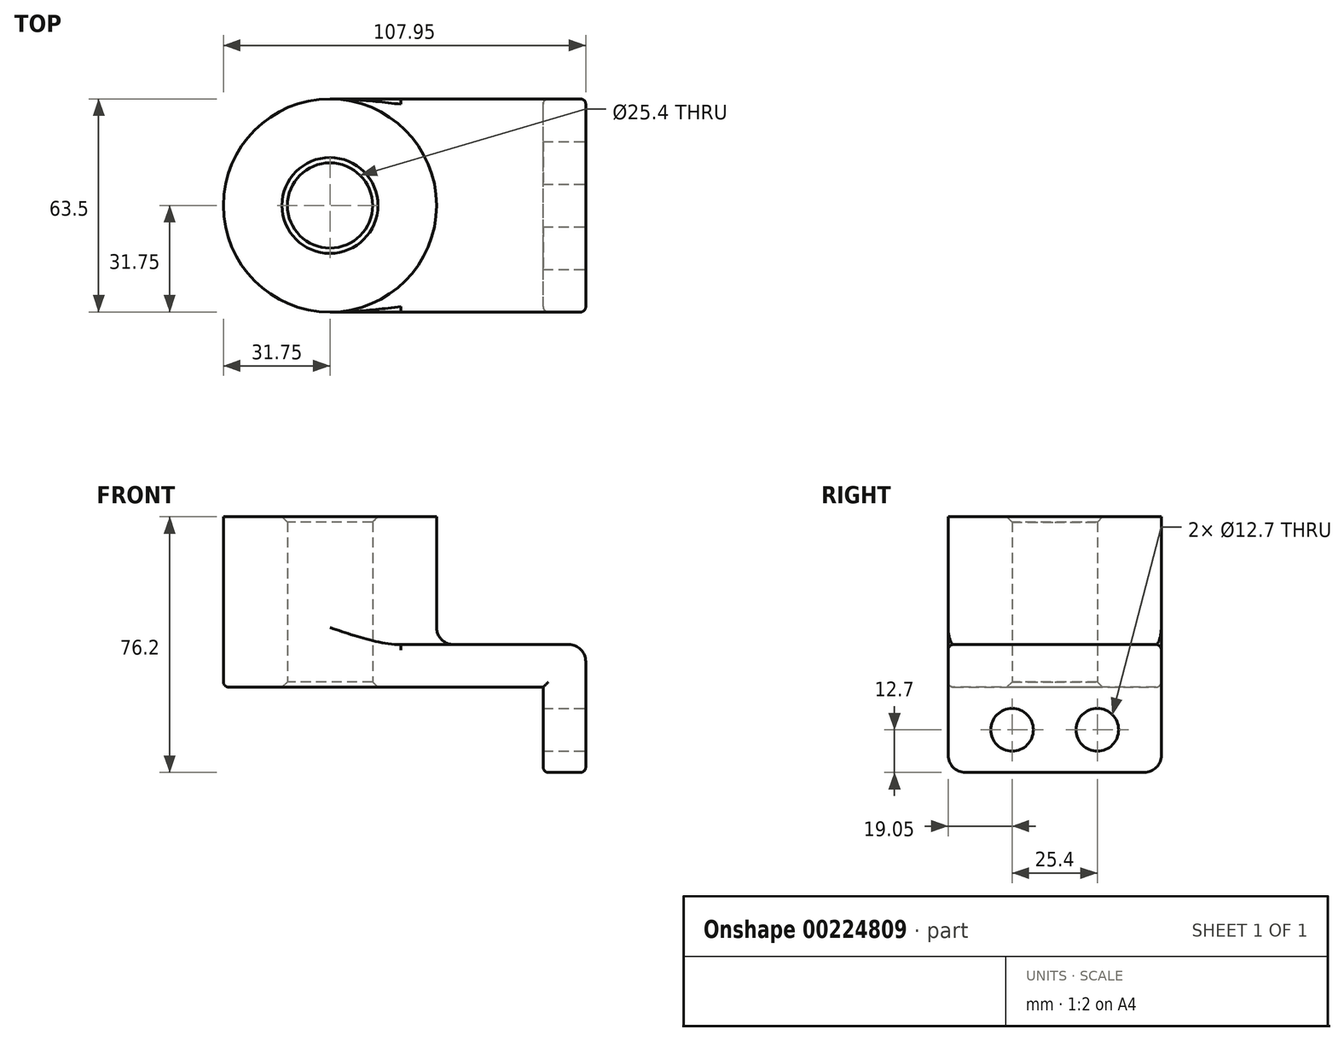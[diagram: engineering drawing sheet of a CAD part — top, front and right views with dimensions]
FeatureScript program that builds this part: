
annotation { "Feature Type Name" : "Feature", "Feature Type Description" : "" }
export const myFeature = defineFeature(function(context is Context, id is Id, definition is map)
    precondition{}
    {
        {
            var Q0;
            Q0=qCreatedBy(makeId("Top.planeOp"),FACE);
            var sketch = newSketch(context, id + "F0", { "sketchPlane" : qUnion([Q0])});
            skLineSegment(sketch, "E0.bottom", {"start": v(38.1, -31.75) * mm, "end": v(-38.1, -31.75) * mm});
            skLineSegment(sketch, "E0.top", {"start": v(38.1, 31.75) * mm, "end": v(-38.1, 31.75) * mm});
            skLineSegment(sketch, "E0.left", {"start": v(38.1, -31.75) * mm, "end": v(38.1, 31.75) * mm});
            skLineSegment(sketch, "E0.right", {"start": v(-38.1, -31.75) * mm, "end": v(-38.1, 31.75) * mm});
            skPoint(sketch, "E0.middle", {"position": v(0, 0) * mm});
            skCircle(sketch, "E1", {"center": v(-38.1, 0) * mm, "radius": 31.75 * mm});
            skCircle(sketch, "E2", {"center": v(-38.1, 0) * mm, "radius": 12.7 * mm});
            skSolve(sketch);
        }
        {
            var Q0;
            Q0 = qSketchRegion(id + "F0", true);
            extrude(context, id + "F1", {"entities" : qUnion([Q0]), "depth" : 12.7 * mm});
        }
        {
            var Q0;
            {var subQ1=sQuery(id+"F0.wireOp",EDGE,"E0.right");var subQ3=sQuery(id+"F0.wireOp",EDGE,"E2");var subQ4=makeQuery(id+"F0.imprint","INTERSECT",VERTEX,{"disambiguationData":[OD(0.0)],"derivedFrom":[subQ1,subQ3]});Q0=makeQuery(id+"F0.imprint","IMPRINT",FACE,{"disambiguationData":[TD([[makeQuery(id+"F0.imprint","IMPRINT",EDGE,{"disambiguationData":[TD([[subQ4,1.0]])],"derivedFrom":subQ3}),-1.0]])]});}
            var Q1;
            {var subQ1=sQuery(id+"F0.wireOp",EDGE,"E0.right");var subQ3=sQuery(id+"F0.wireOp",EDGE,"E2");var subQ4=makeQuery(id+"F0.imprint","INTERSECT",VERTEX,{"disambiguationData":[OD(0.0)],"derivedFrom":[subQ1,subQ3]});Q1=makeQuery(id+"F0.imprint","IMPRINT",FACE,{"disambiguationData":[TD([[makeQuery(id+"F0.imprint","IMPRINT",EDGE,{"disambiguationData":[TD([[subQ4,-1.0]])],"derivedFrom":subQ3}),-1.0]])]});}
            extrude(context, id + "F2", {"entities" : qUnion([Q0, Q1]), "operationType" : NewBodyOperationType.ADD, "depth" : 50.8 * mm});
        }
        {
            var Q0;
            Q0=makeQuery(id+"F1.opExtrude","SWEPT_FACE",FACE,{"disambiguationData":[OSD([sQuery(id+"F0.wireOp",EDGE,"E0.left")])]});
            var sketch = newSketch(context, id + "F3", { "sketchPlane" : qUnion([Q0])});
            skLineSegment(sketch, "E3.bottom", {"start": v(-31.75, 12.7) * mm, "end": v(31.75, 12.7) * mm});
            skLineSegment(sketch, "E3.top", {"start": v(-31.75, -25.4) * mm, "end": v(31.75, -25.4) * mm});
            skLineSegment(sketch, "E3.left", {"start": v(-31.75, 12.7) * mm, "end": v(-31.75, -25.4) * mm});
            skLineSegment(sketch, "E3.right", {"start": v(31.75, 12.7) * mm, "end": v(31.75, -25.4) * mm});
            skCircle(sketch, "E4", {"center": v(-12.7, -12.7) * mm, "radius": 6.35 * mm});
            skLineSegment(sketch, "E5", {"start": v(0, 0) * mm, "end": v(0, -25.4) * mm, "construction": true});
            skCircle(sketch, "E6.MirrorC", {"center": v(12.7, -12.7) * mm, "radius": 6.35 * mm});
            skSolve(sketch);
        }
        {
            var Q0;
            Q0 = qSketchRegion(id + "F3", true);
            extrude(context, id + "F4", {"entities" : qUnion([Q0]), "operationType" : NewBodyOperationType.ADD, "oppositeDirection" : true, "depth" : 12.7 * mm});
        }
        {
            var Q0;
            {var subQ0=sQuery(id+"F0.wireOp",EDGE,"E1");Q0=makeQuery(id+"F2.boolean.opBoolean","INTERSECT",EDGE,{"derivedFrom":[makeQuery(id+"F1.opExtrude","CAP_FACE",FACE,{"disambiguationData":[OSD([sQuery(id+"F0.wireOp",EDGE,"E0.bottom"),sQuery(id+"F0.wireOp",EDGE,"E0.top"),sQuery(id+"F0.wireOp",EDGE,"E0.left"),subQ0,sQuery(id+"F0.wireOp",EDGE,"E2")])],"isStart":false}),makeQuery(id+"F2.opExtrude","SWEPT_FACE",FACE,{"disambiguationData":[OSD([subQ0])]})]});}
            var Q1;
            Q1=makeQuery(id+"F1.opExtrude","CAP_EDGE",EDGE,{"disambiguationData":[OSD([sQuery(id+"F0.wireOp",EDGE,"E0.left")])],"isStart":false});
            var Q2;
            Q2=makeQuery(id+"F4.opExtrude","SWEPT_EDGE",EDGE,{"disambiguationData":[OSD([sQuery(id+"F3.wireOp",EDGE,"E3.top"),sQuery(id+"F3.wireOp",EDGE,"E3.left")])]});
            var Q3;
            Q3=makeQuery(id+"F4.opExtrude","SWEPT_EDGE",EDGE,{"disambiguationData":[OSD([sQuery(id+"F3.wireOp",EDGE,"E3.top"),sQuery(id+"F3.wireOp",EDGE,"E3.right")])]});
            fillet(context, id + "F5", {"entities" : qUnion([Q0, Q1, Q2, Q3]), "radius" : 5.08 * mm, "tangentPropagation" : true, "allowEdgeOverflow" : false});
        }
        {
            var Q0;
            Q0=makeQuery(id+"F1.opExtrude","CAP_EDGE",EDGE,{"disambiguationData":[OSD([sQuery(id+"F0.wireOp",EDGE,"E0.bottom")])],"isStart":false});
            var Q1;
            Q1=makeQuery(id+"F1.opExtrude","CAP_EDGE",EDGE,{"disambiguationData":[OSD([sQuery(id+"F0.wireOp",EDGE,"E0.bottom")])],"isStart":true});
            var Q2;
            Q2=makeQuery(id+"F4.opExtrude","CAP_EDGE",EDGE,{"disambiguationData":[OSD([sQuery(id+"F3.wireOp",EDGE,"E3.left")])],"isStart":false});
            fillet(context, id + "F6", {"entities" : qUnion([Q0, Q1, Q2]), "radius" : 1.59 * mm, "tangentPropagation" : true, "allowEdgeOverflow" : false});
        }
        {
            var Q0;
            Q0=makeQuery(id+"F2.opExtrude","CAP_EDGE",EDGE,{"disambiguationData":[OSD([sQuery(id+"F0.wireOp",EDGE,"E2")])],"isStart":false});
            chamfer(context, id + "F7", {"entities" : qUnion([Q0]), "width" : 1.59 * mm, "tangentPropagation" : true});
        }
        {
            var Q0;
            Q0=makeQuery(id+"F1.opExtrude","CAP_EDGE",EDGE,{"disambiguationData":[OSD([sQuery(id+"F0.wireOp",EDGE,"E2")])],"isStart":true});
            chamfer(context, id + "F8", {"entities" : qUnion([Q0]), "width" : 1.59 * mm, "tangentPropagation" : true});
        }
    });
